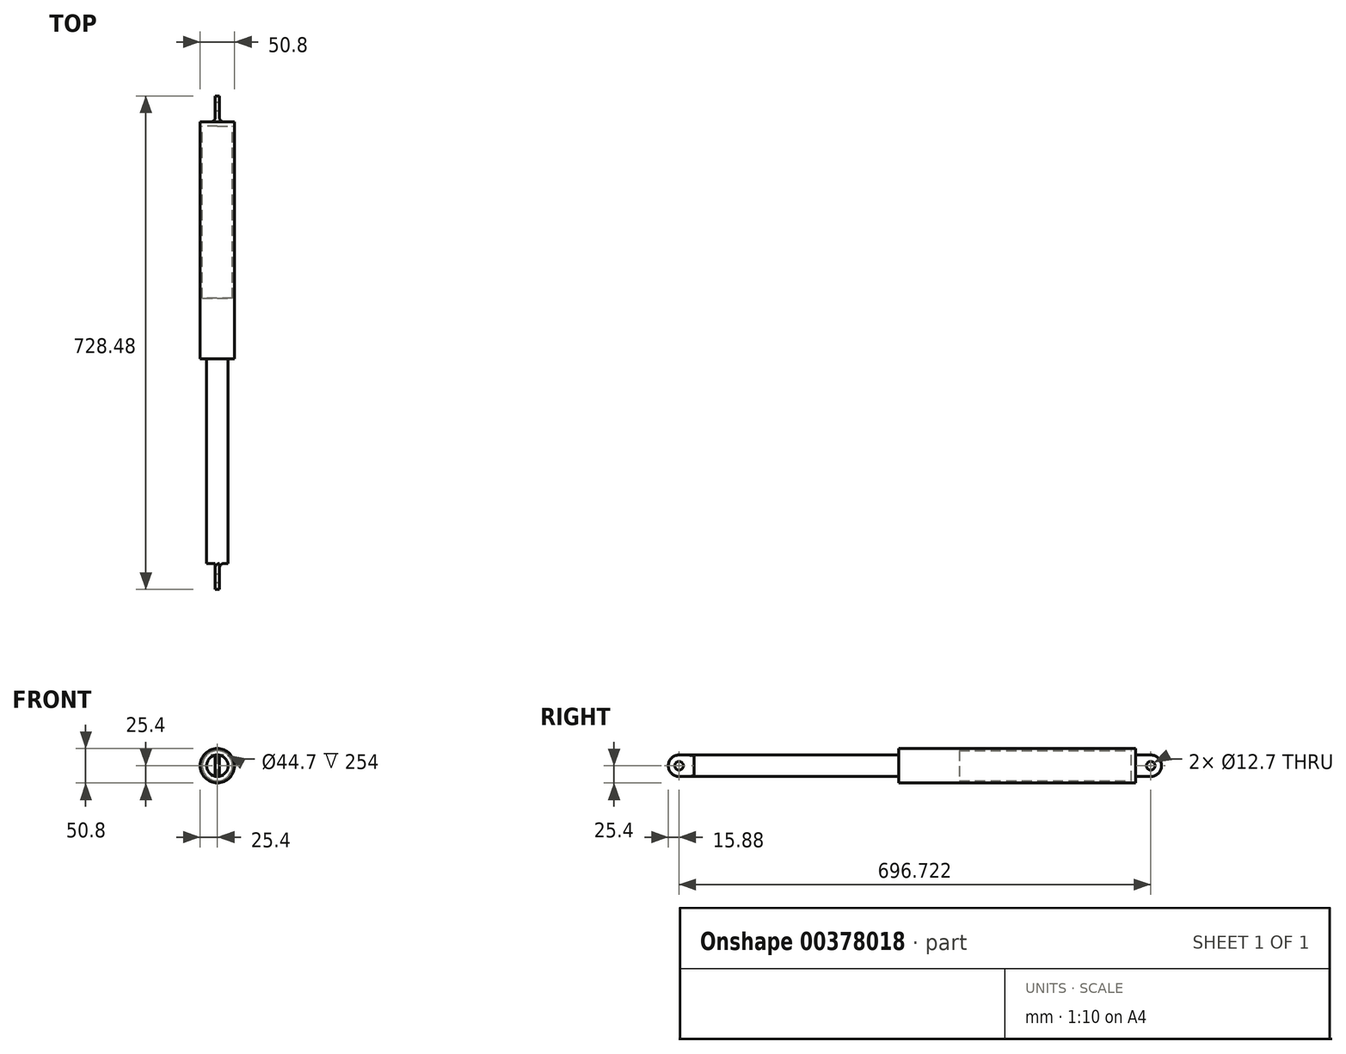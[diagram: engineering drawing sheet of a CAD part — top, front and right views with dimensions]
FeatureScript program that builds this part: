
annotation { "Feature Type Name" : "Feature", "Feature Type Description" : "" }
export const myFeature = defineFeature(function(context is Context, id is Id, definition is map)
    precondition{}
    {
        {
            var Q0;
            Q0=qCreatedBy(makeId("Right.planeOp"),FACE);
            var sketch = newSketch(context, id + "F0", { "sketchPlane" : qUnion([Q0])});
            skArc(sketch, "E0", {"start": v(0, 15.88) * mm, "mid": v(-15.88, 0) * mm, "end": v(0, -15.88) * mm});
            skLineSegment(sketch, "E1", {"start": v(0, 15.88) * mm, "end": v(22.22, 15.88) * mm});
            skLineSegment(sketch, "E2", {"start": v(22.22, 15.88) * mm, "end": v(22.23, -15.88) * mm});
            skCircle(sketch, "E3", {"center": v(0, 0) * mm, "radius": 6.35 * mm});
            skLineSegment(sketch, "E4", {"start": v(0, -15.88) * mm, "end": v(22.23, -15.88) * mm});
            skSolve(sketch);
        }
        {
            var Q0;
            Q0 = qSketchRegion(id + "F0", true);
            extrude(context, id + "F1", {"entities" : qUnion([Q0]), "endBound" : BoundingType.SYMMETRIC, "depth" : 6.35 * mm});
        }
        {
            var Q0;
            Q0=makeQuery(id+"F1.opExtrude","SWEPT_FACE",FACE,{"disambiguationData":[OSD([sQuery(id+"F0.wireOp",EDGE,"E2")])]});
            var sketch = newSketch(context, id + "F2", { "sketchPlane" : qUnion([Q0])});
            skCircle(sketch, "E5", {"center": v(0, 0) * mm, "radius": 15.88 * mm});
            skSolve(sketch);
        }
        {
            var Q0;
            Q0 = qSketchRegion(id + "F2", true);
            extrude(context, id + "F3", {"entities" : qUnion([Q0]), "operationType" : NewBodyOperationType.ADD, "depth" : 375 * mm + 16.92 * mm});
        }
        {
            var Q0;
            {var subQ0=sQuery(id+"F0.wireOp",EDGE,"E2");Q0=makeQuery(id+"F3.boolean.opBoolean","SPLIT",EDGE,{"disambiguationData":[topologyDisambiguationEdgeConnected([makeQuery(id+"F1.opExtrude","CAP_FACE",FACE,{"disambiguationData":[OSD([sQuery(id+"F0.wireOp",EDGE,"E0"),sQuery(id+"F0.wireOp",EDGE,"E1"),subQ0,sQuery(id+"F0.wireOp",EDGE,"E3"),sQuery(id+"F0.wireOp",EDGE,"E4")])],"isStart":false}),makeQuery(id+"F3.opExtrude","CAP_FACE",FACE,{"disambiguationData":[OSD([sQuery(id+"F2.wireOp",EDGE,"E5")])],"isStart":true})])],"derivedFrom":makeQuery(id+"F1.opExtrude","CAP_EDGE",EDGE,{"disambiguationData":[OSD([subQ0])],"isStart":false})});}
            var Q1;
            {var subQ0=sQuery(id+"F0.wireOp",EDGE,"E2");Q1=makeQuery(id+"F3.boolean.opBoolean","SPLIT",EDGE,{"disambiguationData":[topologyDisambiguationEdgeConnected([makeQuery(id+"F1.opExtrude","CAP_FACE",FACE,{"disambiguationData":[OSD([sQuery(id+"F0.wireOp",EDGE,"E0"),sQuery(id+"F0.wireOp",EDGE,"E1"),subQ0,sQuery(id+"F0.wireOp",EDGE,"E3"),sQuery(id+"F0.wireOp",EDGE,"E4")])],"isStart":true}),makeQuery(id+"F3.opExtrude","CAP_FACE",FACE,{"disambiguationData":[OSD([sQuery(id+"F2.wireOp",EDGE,"E5")])],"isStart":true})])],"derivedFrom":makeQuery(id+"F1.opExtrude","CAP_EDGE",EDGE,{"disambiguationData":[OSD([subQ0])],"isStart":true})});}
            fillet(context, id + "F4", {"entities" : qUnion([Q0, Q1]), "radius" : 6.35 * mm, "tangentPropagation" : true, "allowEdgeOverflow" : false});
        }
        {
            var Q0;
            Q0=qCreatedBy(makeId("Right.planeOp"),FACE);
            var sketch = newSketch(context, id + "F5", { "sketchPlane" : qUnion([Q0])});
            skCircle(sketch, "E6", {"center": v(696.72, 0) * mm, "radius": 6.35 * mm});
            skArc(sketch, "E7", {"start": v(696.72, -15.87) * mm, "mid": v(712.6, 0) * mm, "end": v(696.72, 15.88) * mm});
            skLineSegment(sketch, "E8", {"start": v(696.72, 15.88) * mm, "end": v(674.5, 15.88) * mm});
            skLineSegment(sketch, "E9", {"start": v(674.5, 15.88) * mm, "end": v(674.5, -15.88) * mm});
            skLineSegment(sketch, "E10", {"start": v(696.72, -15.88) * mm, "end": v(674.5, -15.88) * mm});
            skSolve(sketch);
        }
        {
            var Q0;
            Q0 = qSketchRegion(id + "F5", true);
            extrude(context, id + "F6", {"entities" : qUnion([Q0]), "endBound" : BoundingType.SYMMETRIC, "depth" : 6.35 * mm});
        }
        {
            var Q0;
            Q0=makeQuery(id+"F6.opExtrude","SWEPT_FACE",FACE,{"disambiguationData":[OSD([sQuery(id+"F5.wireOp",EDGE,"E9")])]});
            var sketch = newSketch(context, id + "F7", { "sketchPlane" : qUnion([Q0])});
            skCircle(sketch, "E11", {"center": v(0, 0) * mm, "radius": 25.4 * mm});
            skCircle(sketch, "E12.0.0", {"center": v(0, 0) * mm, "radius": 15.88 * mm, "construction": true});
            skCircle(sketch, "E13", {"center": v(0, 0) * mm, "radius": 22.35 * mm});
            skSolve(sketch);
        }
        {
            var Q0;
            Q0 = qSketchRegion(id + "F7", true);
            extrude(context, id + "F8", {"entities" : qUnion([Q0]), "depth" : 350 * mm});
        }
        {
            var Q0;
            Q0=makeQuery(id+"F6.opExtrude","SWEPT_FACE",FACE,{"disambiguationData":[OSD([sQuery(id+"F5.wireOp",EDGE,"E9")])]});
            var sketch = newSketch(context, id + "F9", { "sketchPlane" : qUnion([Q0])});
            skCircle(sketch, "E14.0", {"center": v(0, 0) * mm, "radius": 22.35 * mm});
            skSolve(sketch);
        }
        {
            var Q0;
            Q0 = qSketchRegion(id + "F9", true);
            extrude(context, id + "F10", {"entities" : qUnion([Q0]), "operationType" : NewBodyOperationType.ADD, "depth" : 6.35 * mm});
        }
        {
            var Q0;
            {var subQ0=sQuery(id+"F5.wireOp",EDGE,"E9");Q0=makeQuery(id+"F10.boolean.opBoolean","SPLIT",EDGE,{"disambiguationData":[topologyDisambiguationEdgeConnected([makeQuery(id+"F6.opExtrude","CAP_FACE",FACE,{"disambiguationData":[OSD([sQuery(id+"F5.wireOp",EDGE,"E6"),sQuery(id+"F5.wireOp",EDGE,"E7"),sQuery(id+"F5.wireOp",EDGE,"E8"),subQ0,sQuery(id+"F5.wireOp",EDGE,"E10")])],"isStart":true}),makeQuery(id+"F10.opExtrude","CAP_FACE",FACE,{"disambiguationData":[OSD([sQuery(id+"F9.wireOp",EDGE,"0a1f69fb-0a38-4f9e-a69e-4767d570a797.0")])],"isStart":true})])],"derivedFrom":makeQuery(id+"F6.opExtrude","CAP_EDGE",EDGE,{"disambiguationData":[OSD([subQ0])],"isStart":true})});}
            var Q1;
            {var subQ0=sQuery(id+"F5.wireOp",EDGE,"E9");Q1=makeQuery(id+"F10.boolean.opBoolean","SPLIT",EDGE,{"disambiguationData":[topologyDisambiguationEdgeConnected([makeQuery(id+"F6.opExtrude","CAP_FACE",FACE,{"disambiguationData":[OSD([sQuery(id+"F5.wireOp",EDGE,"E6"),sQuery(id+"F5.wireOp",EDGE,"E7"),sQuery(id+"F5.wireOp",EDGE,"E8"),subQ0,sQuery(id+"F5.wireOp",EDGE,"E10")])],"isStart":false}),makeQuery(id+"F10.opExtrude","CAP_FACE",FACE,{"disambiguationData":[OSD([sQuery(id+"F9.wireOp",EDGE,"0a1f69fb-0a38-4f9e-a69e-4767d570a797.0")])],"isStart":true})])],"derivedFrom":makeQuery(id+"F6.opExtrude","CAP_EDGE",EDGE,{"disambiguationData":[OSD([subQ0])],"isStart":false})});}
            fillet(context, id + "F11", {"entities" : qUnion([Q0, Q1]), "radius" : 6.35 * mm, "tangentPropagation" : true, "allowEdgeOverflow" : false});
        }
        {
            var Q0;
            Q0=makeQuery(id+"F8.opExtrude","CAP_FACE",FACE,{"disambiguationData":[OSD([sQuery(id+"F7.wireOp",EDGE,"E11"),sQuery(id+"F7.wireOp",EDGE,"E13")])],"isStart":false});
            var sketch = newSketch(context, id + "F12", { "sketchPlane" : qUnion([Q0])});
            skCircle(sketch, "E15.0", {"center": v(0, 0) * mm, "radius": 22.35 * mm});
            skCircle(sketch, "E16.0", {"center": v(0, 0) * mm, "radius": 15.88 * mm});
            skSolve(sketch);
        }
        {
            var Q0;
            Q0 = qSketchRegion(id + "F12", true);
            extrude(context, id + "F13", {"entities" : qUnion([Q0]), "operationType" : NewBodyOperationType.ADD, "oppositeDirection" : true, "depth" : 6.35 * mm});
        }
        {
            var Q0;
            Q0=makeQuery(id+"F3.opExtrude","CAP_FACE",FACE,{"disambiguationData":[OSD([sQuery(id+"F2.wireOp",EDGE,"E5")])],"isStart":false});
            var sketch = newSketch(context, id + "F14", { "sketchPlane" : qUnion([Q0])});
            skCircle(sketch, "E17.0", {"center": v(0, 0) * mm, "radius": 25.4 * mm, "construction": true});
            skCircle(sketch, "E18", {"center": v(0, 0) * mm, "radius": 22.35 * mm});
            skCircle(sketch, "E19.0", {"center": v(0, 0) * mm, "radius": 15.88 * mm});
            skSolve(sketch);
        }
        {
            var Q0;
            Q0 = qSketchRegion(id + "F14", true);
            extrude(context, id + "F15", {"entities" : qUnion([Q0]), "operationType" : NewBodyOperationType.ADD, "endBound" : BoundingType.UP_TO_NEXT, "oppositeDirection" : true, "depth" : 25 * mm});
        }
    });
